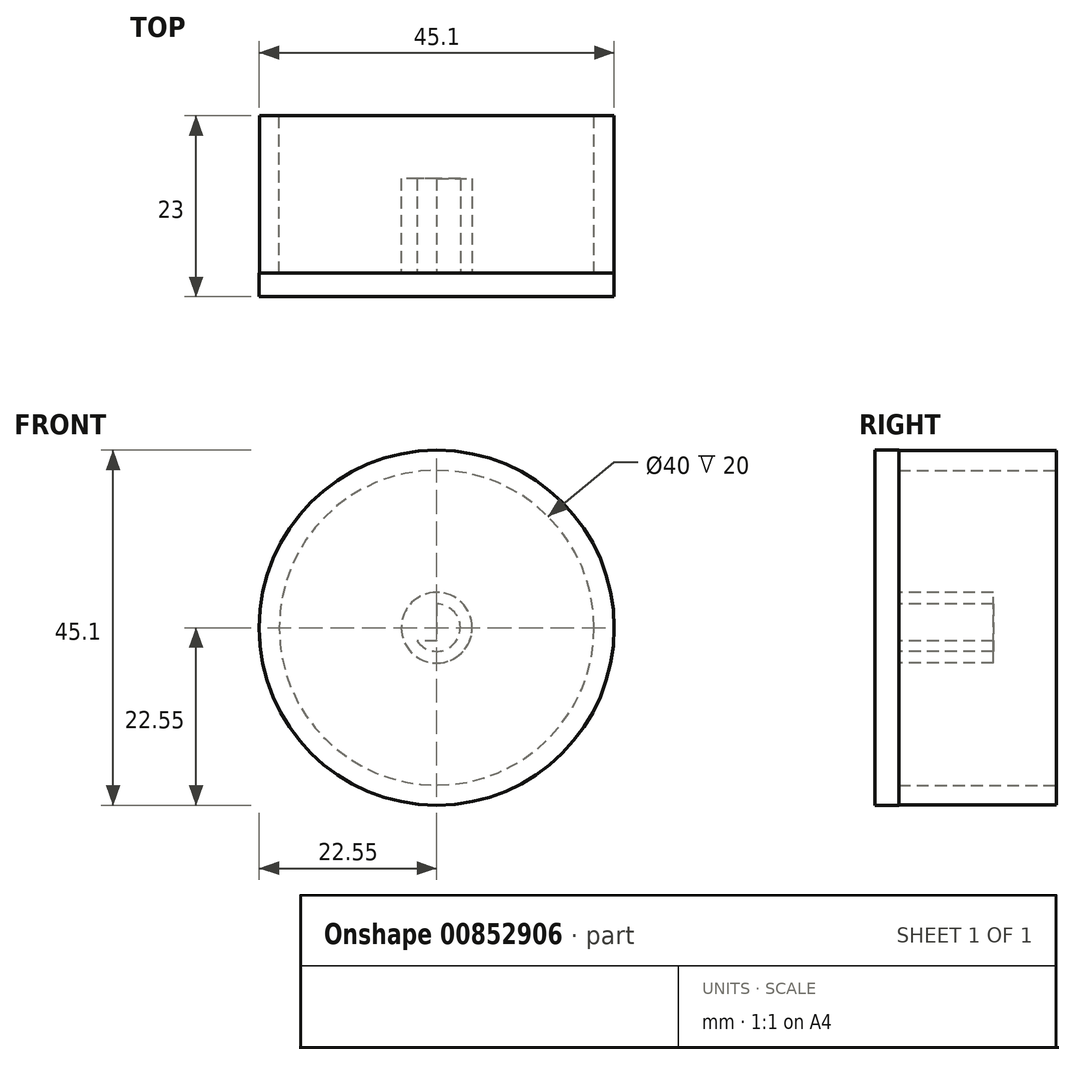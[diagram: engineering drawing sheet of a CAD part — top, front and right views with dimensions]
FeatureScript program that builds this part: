
annotation { "Feature Type Name" : "Feature", "Feature Type Description" : "" }
export const myFeature = defineFeature(function(context is Context, id is Id, definition is map)
    precondition{}
    {
        {
            var Q0;
            Q0=qCreatedBy(makeId("Front.planeOp"),FACE);
            var sketch = newSketch(context, id + "F0", { "sketchPlane" : qUnion([Q0])});
            skCircle(sketch, "E0", {"center": v(0, 0) * mm, "radius": 22.5 * mm});
            skCircle(sketch, "E1", {"center": v(0, 0) * mm, "radius": 20 * mm});
            skSolve(sketch);
        }
        {
            var Q0;
            Q0=makeQuery(id+"F0.imprint","IMPRINT",FACE,{"disambiguationData":[TD([[makeQuery(id+"F0.imprint","IMPRINT",EDGE,{"derivedFrom":sQuery(id+"F0.wireOp",EDGE,"E0")}),1.0]])]});
            extrude(context, id + "F1", {"entities" : qUnion([Q0]), "depth" : 20 * mm, "offsetDistance" : 25 * mm});
        }
        {
            var Q0;
            Q0=makeQuery(id+"F1.opExtrude","CAP_FACE",FACE,{"disambiguationData":[OSD([sQuery(id+"F0.wireOp",EDGE,"E0"),sQuery(id+"F0.wireOp",EDGE,"E1")])],"isStart":false});
            var sketch = newSketch(context, id + "F2", { "sketchPlane" : qUnion([Q0])});
            skCircle(sketch, "E2", {"center": v(0, 0) * mm, "radius": 22.55 * mm});
            skSolve(sketch);
        }
        {
            var Q0;
            Q0 = qSketchRegion(id + "F2", true);
            extrude(context, id + "F3", {"entities" : qUnion([Q0]), "operationType" : NewBodyOperationType.ADD, "depth" : 3 * mm, "offsetDistance" : 25 * mm});
        }
        {
            var Q0;
            Q0=makeQuery(id+"F3.boolean.opBoolean","SPLIT",FACE,{"disambiguationData":[TD([makeQuery(id+"F1.opExtrude","SWEPT_FACE",FACE,{"disambiguationData":[OSD([sQuery(id+"F0.wireOp",EDGE,"E1")])]})])],"derivedFrom":makeQuery(id+"F3.opExtrude","CAP_FACE",FACE,{"disambiguationData":[OSD([sQuery(id+"F2.wireOp",EDGE,"E2")])],"isStart":true})});
            var sketch = newSketch(context, id + "F4", { "sketchPlane" : qUnion([Q0])});
            skCircle(sketch, "E3", {"center": v(0, 0) * mm, "radius": 3 * mm});
            skLineSegment(sketch, "E4", {"start": v(0, 3) * mm, "end": v(0, -1.7) * mm});
            skLineSegment(sketch, "E5", {"start": v(0, -1.7) * mm, "end": v(-2.47, -1.7) * mm});
            skLineSegment(sketch, "E6", {"start": v(-2.47, -1.7) * mm, "end": v(2.47, -1.7) * mm});
            skCircle(sketch, "E7", {"center": v(0, 0) * mm, "radius": 4.5 * mm});
            skSolve(sketch);
        }
        {
            var Q0;
            Q0=makeQuery(id+"F4.imprint","IMPRINT",FACE,{"disambiguationData":[TD([[makeQuery(id+"F4.imprint","IMPRINT",EDGE,{"derivedFrom":sQuery(id+"F4.wireOp",EDGE,"E7")}),1.0]])]});
            var Q1;
            {var subQ0=sQuery(id+"F4.wireOp",EDGE,"E6");var subQ1=sQuery(id+"F4.wireOp",EDGE,"E3");var subQ2=makeQuery(id+"F4.imprint","INTERSECT",VERTEX,{"disambiguationData":[OD(0.0)],"derivedFrom":[subQ1,subQ0]});Q1=makeQuery(id+"F4.imprint","IMPRINT",FACE,{"disambiguationData":[TD([[makeQuery(id+"F4.imprint","IMPRINT",EDGE,{"disambiguationData":[TD([[subQ2,-1.0]])],"derivedFrom":subQ1}),1.0]])]});}
            extrude(context, id + "F5", {"entities" : qUnion([Q0, Q1]), "operationType" : NewBodyOperationType.ADD, "depth" : 12 * mm, "offsetDistance" : 25 * mm});
        }
    });
